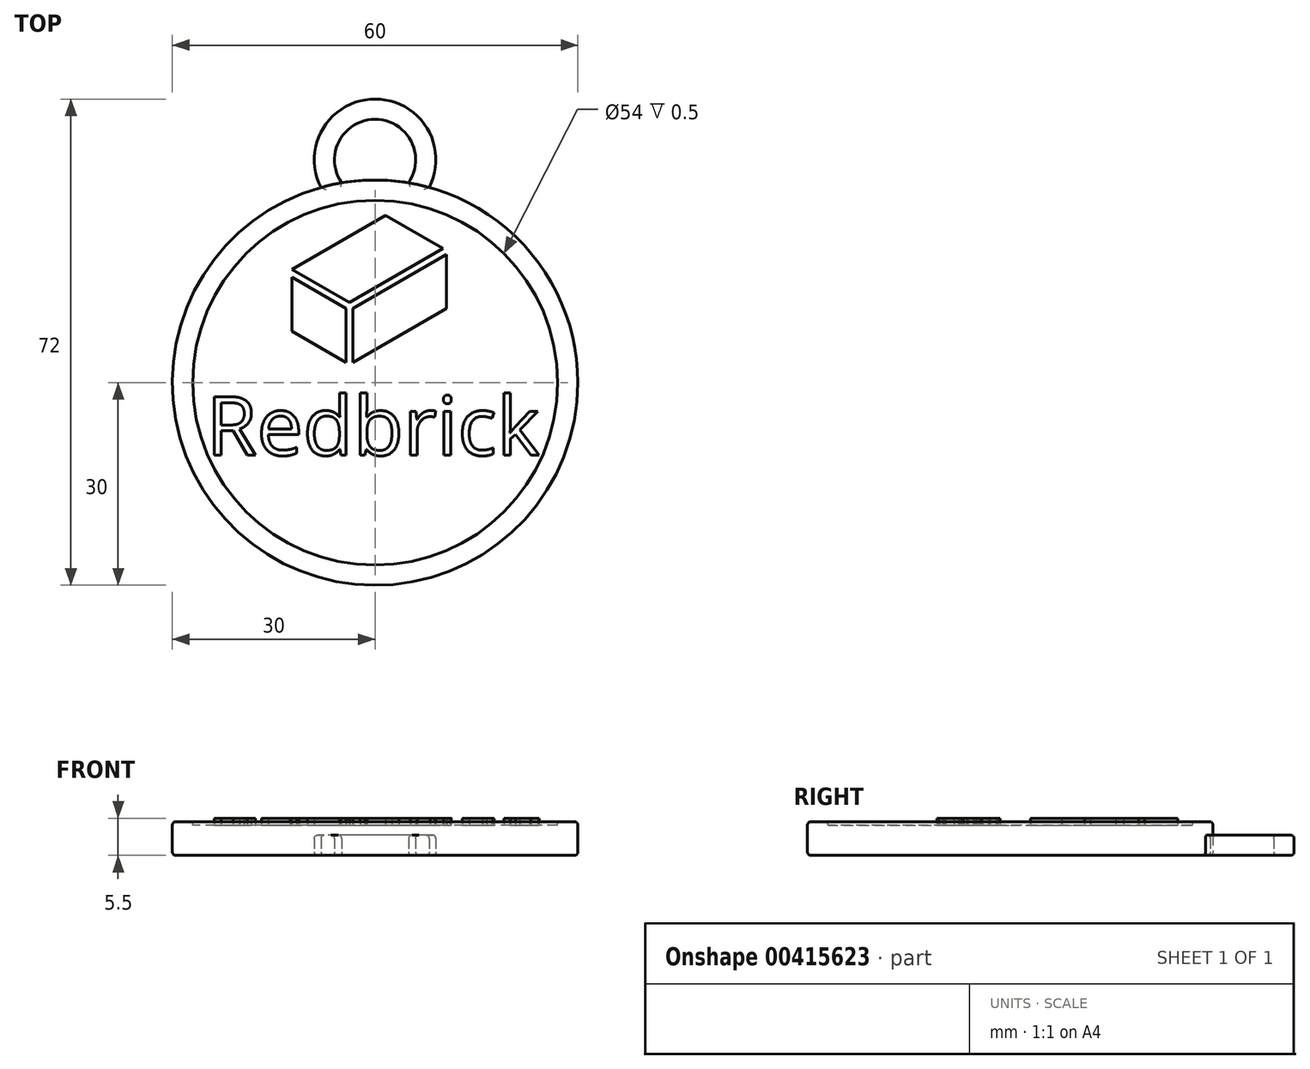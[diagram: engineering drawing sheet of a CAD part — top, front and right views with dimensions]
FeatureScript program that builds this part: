
annotation { "Feature Type Name" : "Feature", "Feature Type Description" : "" }
export const myFeature = defineFeature(function(context is Context, id is Id, definition is map)
    precondition{}
    {
        {
            var Q0;
            Q0=qCreatedBy(makeId("Top.planeOp"),FACE);
            var sketch = newSketch(context, id + "F0", { "sketchPlane" : qUnion([Q0])});
            skCircle(sketch, "E0", {"center": v(0, 0) * mm, "radius": 30 * mm});
            skSolve(sketch);
        }
        {
            var Q0;
            Q0 = qSketchRegion(id + "F0", true);
            extrude(context, id + "F1", {"entities" : qUnion([Q0]), "depth" : 5 * mm});
        }
        {
            var Q0;
            Q0=makeQuery(id+"F1.opExtrude","CAP_FACE",FACE,{"disambiguationData":[OSD([sQuery(id+"F0.wireOp",EDGE,"E0")])],"isStart":false});
            var sketch = newSketch(context, id + "F2", { "sketchPlane" : qUnion([Q0])});
            skCircle(sketch, "E1", {"center": v(0, 0) * mm, "radius": 27 * mm});
            skSolve(sketch);
        }
        {
            var Q0;
            Q0 = qSketchRegion(id + "F2", true);
            extrude(context, id + "F3", {"entities" : qUnion([Q0]), "operationType" : NewBodyOperationType.REMOVE, "oppositeDirection" : true, "depth" : .5 * mm});
        }
        {
            var Q0;
            Q0=makeQuery(id+"F3.boolean.opBoolean","COPY",FACE,{"derivedFrom":makeQuery(id+"F3.opExtrude","CAP_FACE",FACE,{"disambiguationData":[OSD([sQuery(id+"F2.wireOp",EDGE,"E1")])],"isStart":false})});
            var sketch = newSketch(context, id + "F4", { "sketchPlane" : qUnion([Q0])});
            skText(sketch, "E2", { "text": "Redbrick", "fontName": "OpenSans-Regular.ttf"});
            const initialGuessF4  = {"E2": [-0.025, -0.01074, 1, 0, 0.00874]};
            skSetInitialGuess(sketch, initialGuessF4);
            skSolve(sketch);
        }
        {
            var Q0;
            Q0 = qSketchRegion(id + "F4", true);
            extrude(context, id + "F5", {"entities" : qUnion([Q0]), "operationType" : NewBodyOperationType.ADD, "depth" : 1 * mm});
        }
        {
            var Q0;
            {var subQ0=sQuery(id+"F2.wireOp",EDGE,"E1");Q0=makeQuery(id+"F5.boolean.opBoolean","SPLIT",FACE,{"disambiguationData":[TD([makeQuery(id+"F3.boolean.opBoolean","COPY",FACE,{"derivedFrom":makeQuery(id+"F3.opExtrude","SWEPT_FACE",FACE,{"disambiguationData":[OSD([subQ0])]})})])],"derivedFrom":makeQuery(id+"F3.boolean.opBoolean","COPY",FACE,{"derivedFrom":makeQuery(id+"F3.opExtrude","CAP_FACE",FACE,{"disambiguationData":[OSD([subQ0])],"isStart":false})})});}
            var sketch = newSketch(context, id + "F6", { "sketchPlane" : qUnion([Q0])});
            skLineSegment(sketch, "E3", {"start": v(-4.3, 3) * mm, "end": v(-12.3, 7.62) * mm});
            skLineSegment(sketch, "E4", {"start": v(-12.3, 7.62) * mm, "end": v(-12.3, 15.62) * mm});
            skLineSegment(sketch, "E5", {"start": v(-12.3, 15.62) * mm, "end": v(-4.3, 11) * mm});
            skLineSegment(sketch, "E6", {"start": v(-4.3, 11) * mm, "end": v(-4.3, 3) * mm});
            skLineSegment(sketch, "E7", {"start": v(-3.3, 3) * mm, "end": v(-3.3, 11) * mm});
            skLineSegment(sketch, "E8", {"start": v(-3.3, 11) * mm, "end": v(10.55, 19) * mm});
            skLineSegment(sketch, "E9", {"start": v(10.55, 19) * mm, "end": v(10.55, 11) * mm});
            skLineSegment(sketch, "E10", {"start": v(10.55, 11) * mm, "end": v(-3.3, 3) * mm});
            skLineSegment(sketch, "E11", {"start": v(-12.3, 16.77) * mm, "end": v(-3.8, 11.87) * mm});
            skLineSegment(sketch, "E12", {"start": v(-3.8, 11.87) * mm, "end": v(10.05, 19.87) * mm});
            skLineSegment(sketch, "E13", {"start": v(10.05, 19.87) * mm, "end": v(1.55, 24.77) * mm});
            skLineSegment(sketch, "E14", {"start": v(1.55, 24.77) * mm, "end": v(-12.3, 16.77) * mm});
            skSolve(sketch);
        }
        {
            var Q0;
            Q0 = qSketchRegion(id + "F6", true);
            extrude(context, id + "F7", {"entities" : qUnion([Q0]), "operationType" : NewBodyOperationType.ADD, "depth" : 1 * mm});
        }
        {
            var Q0;
            Q0=qCreatedBy(makeId("Top.planeOp"),FACE);
            var sketch = newSketch(context, id + "F8", { "sketchPlane" : qUnion([Q0])});
            skCircle(sketch, "E15", {"center": v(0, 33) * mm, "radius": 9 * mm});
            skCircle(sketch, "E16", {"center": v(0, 33) * mm, "radius": 6 * mm});
            skSolve(sketch);
        }
        {
            var Q0;
            Q0=makeQuery(id+"F8.imprint","IMPRINT",FACE,{"disambiguationData":[TD([[makeQuery(id+"F8.imprint","IMPRINT",EDGE,{"derivedFrom":sQuery(id+"F8.wireOp",EDGE,"E15")}),1.0]])]});
            extrude(context, id + "F9", {"entities" : qUnion([Q0]), "operationType" : NewBodyOperationType.ADD, "depth" : 3 * mm});
        }
        {
            var Q0;
            Q0=makeQuery(id+"F1.opExtrude","CAP_EDGE",EDGE,{"disambiguationData":[OSD([sQuery(id+"F0.wireOp",EDGE,"E0")])],"isStart":false});
            var Q1;
            Q1=makeQuery(id+"F3.boolean.opBoolean","COPY",EDGE,{"derivedFrom":makeQuery(id+"F3.opExtrude","CAP_EDGE",EDGE,{"disambiguationData":[OSD([sQuery(id+"F2.wireOp",EDGE,"E1")])],"isStart":true})});
            var Q2;
            {var subQ0=sQuery(id+"F0.wireOp",EDGE,"E0");var subQ1=sQuery(id+"F8.wireOp",EDGE,"E15");Q2=makeQuery(id+"F9.boolean.opBoolean","SPLIT",EDGE,{"disambiguationData":[TD([makeQuery(id+"F9.opExtrude","SWEPT_FACE",FACE,{"disambiguationData":[OSD([subQ1])]})])],"derivedFrom":makeQuery(id+"F1.opExtrude","CAP_EDGE",EDGE,{"disambiguationData":[OSD([subQ0])],"isStart":true})});}
            var Q3;
            Q3=makeQuery(id+"F9.opExtrude","CAP_EDGE",EDGE,{"disambiguationData":[OSD([sQuery(id+"F8.wireOp",EDGE,"E16")])],"isStart":false});
            var Q4;
            Q4=makeQuery(id+"F9.opExtrude","CAP_EDGE",EDGE,{"disambiguationData":[OSD([sQuery(id+"F8.wireOp",EDGE,"E15")])],"isStart":false});
            var Q5;
            Q5=makeQuery(id+"F9.opExtrude","CAP_EDGE",EDGE,{"disambiguationData":[OSD([sQuery(id+"F8.wireOp",EDGE,"E15")])],"isStart":true});
            var Q6;
            Q6=makeQuery(id+"F9.opExtrude","CAP_EDGE",EDGE,{"disambiguationData":[OSD([sQuery(id+"F8.wireOp",EDGE,"E16")])],"isStart":true});
            var Q7;
            {var subQ0=sQuery(id+"F0.wireOp",EDGE,"E0");var subQ1=sQuery(id+"F8.wireOp",EDGE,"E16");Q7=makeQuery(id+"F9.boolean.opBoolean","SPLIT",EDGE,{"disambiguationData":[TD([makeQuery(id+"F9.opExtrude","SWEPT_FACE",FACE,{"disambiguationData":[OSD([subQ1])]})])],"derivedFrom":makeQuery(id+"F1.opExtrude","CAP_EDGE",EDGE,{"disambiguationData":[OSD([subQ0])],"isStart":true})});}
            fillet(context, id + "F10", {"entities" : qUnion([Q0, Q1, Q2, Q3, Q4, Q5, Q6, Q7]), "radius" : .5 * mm, "tangentPropagation" : true, "allowEdgeOverflow" : false});
        }
    });
